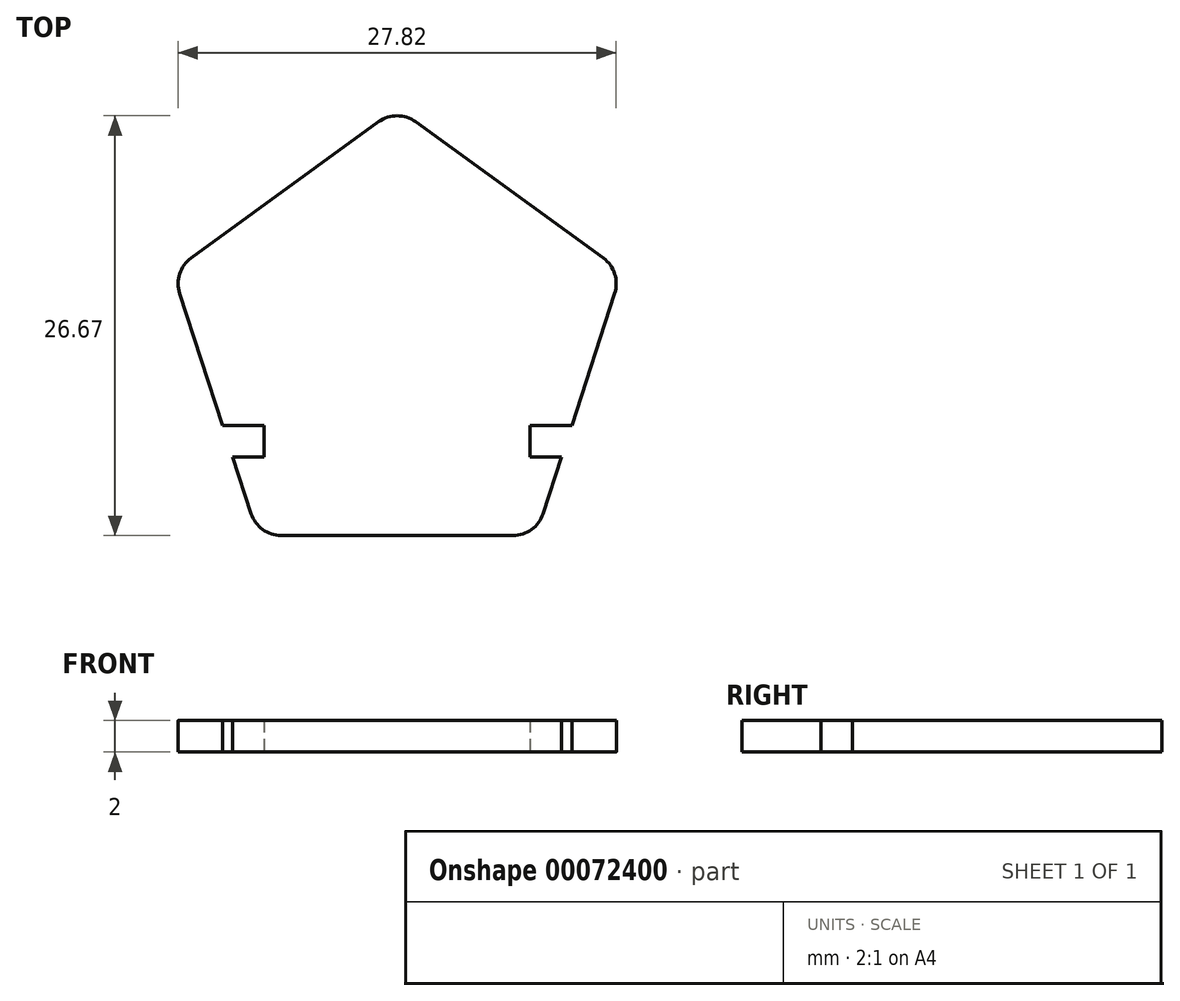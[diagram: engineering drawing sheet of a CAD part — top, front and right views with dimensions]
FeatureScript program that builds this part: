
annotation { "Feature Type Name" : "Feature", "Feature Type Description" : "" }
export const myFeature = defineFeature(function(context is Context, id is Id, definition is map)
    precondition{}
    {
        {
            var Q0;
            Q0=qCreatedBy(makeId("Top.planeOp"),FACE);
            var sketch = newSketch(context, id + "F0", { "sketchPlane" : qUnion([Q0])});
            skCircle(sketch, "E0.cCircle", {"center": v(0, 0) * mm, "radius": 15 * mm, "construction": true});
            skLineSegment(sketch, "E0.0", {"start": v(1.18, 14.15) * mm, "end": v(13.1, 5.49) * mm});
            skLineSegment(sketch, "E0.1", {"start": v(13.82, 3.25) * mm, "end": v(11.1, -5.14) * mm});
            skLineSegment(sketch, "E0.2", {"start": v(7.36, -12.14) * mm, "end": v(-7.36, -12.14) * mm});
            skLineSegment(sketch, "E0.3", {"start": v(-9.27, -10.75) * mm, "end": v(-10.44, -7.14) * mm});
            skLineSegment(sketch, "E0.4", {"start": v(-13.1, 5.49) * mm, "end": v(-1.18, 14.15) * mm});
            skPoint(sketch, "E1.visualSharp", {"position": v(0, 15) * mm});
            skArc(sketch, "E1.filletArc", {"start": v(1.18, 14.15) * mm, "mid": v(0, 14.53) * mm, "end": v(-1.18, 14.15) * mm});
            skPoint(sketch, "E2.visualSharp", {"position": v(14.27, 4.64) * mm});
            skArc(sketch, "E2.filletArc", {"start": v(13.82, 3.25) * mm, "mid": v(13.82, 4.49) * mm, "end": v(13.1, 5.49) * mm});
            skPoint(sketch, "E3.visualSharp", {"position": v(8.82, -12.14) * mm});
            skArc(sketch, "E3.filletArc", {"start": v(7.36, -12.14) * mm, "mid": v(8.54, -11.75) * mm, "end": v(9.27, -10.75) * mm});
            skPoint(sketch, "E4.visualSharp", {"position": v(-8.82, -12.14) * mm});
            skArc(sketch, "E4.filletArc", {"start": v(-9.27, -10.75) * mm, "mid": v(-8.54, -11.75) * mm, "end": v(-7.36, -12.14) * mm});
            skPoint(sketch, "E5.visualSharp", {"position": v(-14.27, 4.64) * mm});
            skArc(sketch, "E5.filletArc", {"start": v(-13.1, 5.49) * mm, "mid": v(-13.82, 4.49) * mm, "end": v(-13.82, 3.25) * mm});
            skPoint(sketch, "E6", {"position": v(8.44, -7.14) * mm});
            skLineSegment(sketch, "E7", {"start": v(8.44, -7.14) * mm, "end": v(8.44, -5.14) * mm});
            skPoint(sketch, "E8", {"position": v(-8.44, -7.14) * mm});
            skLineSegment(sketch, "E9", {"start": v(-8.44, -7.14) * mm, "end": v(-8.44, -5.14) * mm});
            skLineSegment(sketch, "E10", {"start": v(-8.44, -7.14) * mm, "end": v(-10.44, -7.14) * mm});
            skLineSegment(sketch, "E11", {"start": v(-8.44, -5.14) * mm, "end": v(-11.1, -5.14) * mm});
            skLineSegment(sketch, "E12", {"start": v(8.44, -7.14) * mm, "end": v(10.44, -7.14) * mm});
            skLineSegment(sketch, "E13", {"start": v(8.44, -5.14) * mm, "end": v(11.1, -5.14) * mm});
            skLineSegment(sketch, "E14.trimOffspring", {"start": v(10.44, -7.14) * mm, "end": v(9.27, -10.75) * mm});
            skLineSegment(sketch, "E15.trimOffspring", {"start": v(-11.1, -5.14) * mm, "end": v(-13.82, 3.25) * mm});
            skPoint(sketch, "E16.endSnap0", {"position": v(0, 14.53) * mm});
            skSolve(sketch);
        }
        {
            var Q0;
            Q0=makeQuery(id+"F0.imprint","IMPRINT",FACE,{"disambiguationData":[TD([[makeQuery(id+"F0.imprint","IMPRINT",EDGE,{"derivedFrom":sQuery(id+"F0.wireOp",EDGE,"E0.0")}),-1.0]])]});
            extrude(context, id + "F1", {"entities" : qUnion([Q0]), "depth" : 2 * mm});
        }
    });
